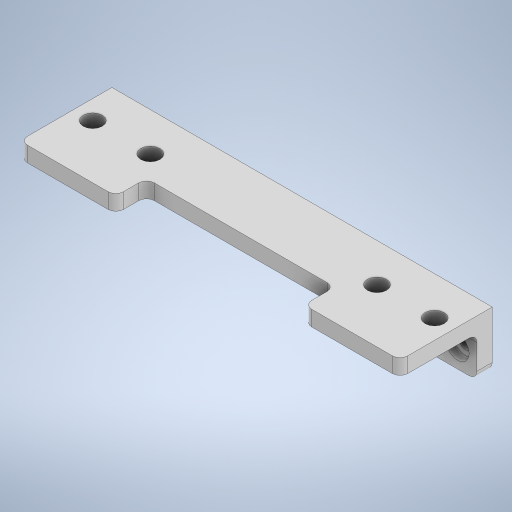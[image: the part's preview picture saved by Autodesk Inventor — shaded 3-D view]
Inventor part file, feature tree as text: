
AUTODESK INVENTOR PART (.ipt)
format: ipt  version: 2024.3 (Build 283343000, 343)  size: 384,000 bytes
history: native  units: mm
features: sketch x9, extrude x8, projected_geometry x4, fillet x2, other x1, hole x1
ambient origin geometry x8: Origin, YZ Plane, XZ Plane, XY Plane, X Axis, Y Axis, Z Axis, Center Point
bodies: Body1 (feature_tree)
feature tree (25):
  other  "ソリッド1"
  extrude  "押し出し1"  Depth=3.2mm
  extrude  "押し出し2"  Depth=3.2mm
  hole  "穴1"  [1 undecoded]
  extrude  "押し出し3"  Depth=5.0mm
  extrude  "押し出し4"  Depth=5.0mm
  extrude  "押し出し5"  Depth=9.5mm
  fillet  "フィレット1"  Radius=14.5mm
  extrude  "押し出し6"  Depth=9.5mm
  extrude  "押し出し7"  Depth=4.0mm TaperAngle=0.0deg
  fillet  "フィレット2"  Radius=4.0mm
  extrude  "押し出し8"  Depth=20.0mm TaperAngle=0.0deg
  sketch  "スケッチ1"
  sketch  "スケッチ2"
  sketch  "スケッチ3"
  sketch  "スケッチ4"
  projected_geometry  "投影ループ1"
  sketch  "スケッチ5"
  sketch  "スケッチ6"
  sketch  "スケッチ8"
  sketch  "スケッチ9"
  projected_geometry  "投影ループ2"
  sketch  "スケッチ10"
  projected_geometry  "投影ループ3"
  projected_geometry  "投影ループ4"
note: 1 required parameter value undecoded (feature->parameter linkage not recoverable at this tier; creation-order binding heuristic only, values carry confidence <= 0.55)
